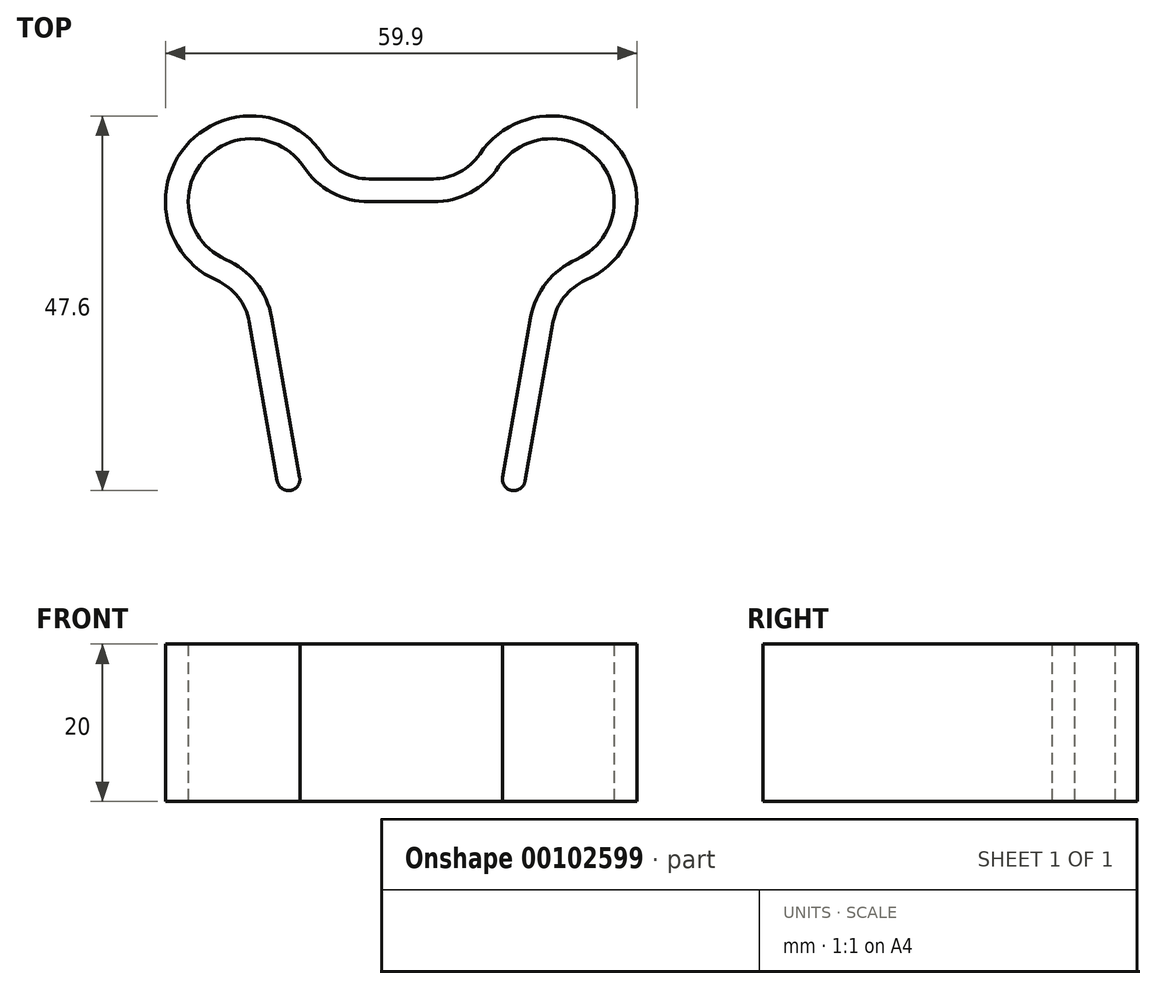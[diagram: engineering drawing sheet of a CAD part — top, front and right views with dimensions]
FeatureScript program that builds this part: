
annotation { "Feature Type Name" : "Feature", "Feature Type Description" : "" }
export const myFeature = defineFeature(function(context is Context, id is Id, definition is map)
    precondition{}
    {
        {
            var Q0;
            Q0=qCreatedBy(makeId("Top.planeOp"),FACE);
            var sketch = newSketch(context, id + "F0", { "sketchPlane" : qUnion([Q0])});
            skLineSegment(sketch, "E0.bottom", {"start": v(-19.05, 18.35) * mm, "end": v(19.05, 18.35) * mm, "construction": true});
            skLineSegment(sketch, "E0.top", {"start": v(-19.05, -18.35) * mm, "end": v(19.05, -18.35) * mm, "construction": true});
            skLineSegment(sketch, "E0.left", {"start": v(-19.05, 18.35) * mm, "end": v(-19.05, -18.35) * mm, "construction": true});
            skLineSegment(sketch, "E0.right", {"start": v(19.05, 18.35) * mm, "end": v(19.05, -18.35) * mm, "construction": true});
            skPoint(sketch, "E0.middle", {"position": v(0, 0) * mm});
            skLineSegment(sketch, "E1", {"start": v(0, 0) * mm, "end": v(0, 18.35) * mm, "construction": true});
            skLineSegment(sketch, "E2", {"start": v(0, 18.35) * mm, "end": v(-4.08, 18.35) * mm});
            skArc(sketch, "E3", {"start": v(-12.4, 22.8) * mm, "mid": v(-25.18, 23.5) * mm, "end": v(-22.27, 11.03) * mm});
            skLineSegment(sketch, "E4", {"start": v(-16.45, 3.61) * mm, "end": v(-12.88, -16.65) * mm});
            skArc(sketch, "E5", {"start": v(-15.73, -17.15) * mm, "mid": v(-14.05, -18.33) * mm, "end": v(-12.88, -16.65) * mm});
            skPoint(sketch, "E6.visualSharp", {"position": v(-19.56, 20.86) * mm});
            skPoint(sketch, "E7.visualSharp", {"position": v(-17.66, 10.47) * mm});
            skArc(sketch, "E7.filletArc", {"start": v(-16.45, 3.61) * mm, "mid": v(-18.43, 8.05) * mm, "end": v(-22.27, 11.03) * mm});
            skPoint(sketch, "E8.visualSharp", {"position": v(-11.05, 18.35) * mm});
            skArc(sketch, "E8.filletArc", {"start": v(-12.4, 22.8) * mm, "mid": v(-8.8, 19.53) * mm, "end": v(-4.08, 18.35) * mm});
            skPoint(sketch, "E9.visualSharp", {"position": v(-9, 35.61) * mm});
            skLineSegment(sketch, "E10", {"start": v(-19.05, 18.35) * mm, "end": v(-12.88, -16.65) * mm, "construction": true});
            skLineSegment(sketch, "E11", {"start": v(-15.73, -17.15) * mm, "end": v(-12.88, -16.65) * mm, "construction": true});
            skLineSegment(sketch, "E12.0", {"start": v(-19.3, 3.1) * mm, "end": v(-15.73, -17.15) * mm});
            skLineSegment(sketch, "E12.1", {"start": v(0, 21.25) * mm, "end": v(-4.08, 21.25) * mm});
            skArc(sketch, "E12.2", {"start": v(-9.99, 24.4) * mm, "mid": v(-7.43, 22.09) * mm, "end": v(-4.08, 21.25) * mm});
            skArc(sketch, "E12.3", {"start": v(-9.99, 24.4) * mm, "mid": v(-27.4, 25.36) * mm, "end": v(-23.44, 8.37) * mm});
            skArc(sketch, "E12.4", {"start": v(-19.3, 3.1) * mm, "mid": v(-20.71, 6.26) * mm, "end": v(-23.44, 8.37) * mm});
            skLineSegment(sketch, "E13.MirrorCS", {"start": v(15.73, -17.15) * mm, "end": v(12.88, -16.65) * mm, "construction": true});
            skArc(sketch, "E14.MirrorCS", {"start": v(9.99, 24.4) * mm, "mid": v(27.4, 25.36) * mm, "end": v(23.44, 8.37) * mm});
            skArc(sketch, "E15.MirrorCS", {"start": v(9.99, 24.4) * mm, "mid": v(7.43, 22.09) * mm, "end": v(4.08, 21.25) * mm});
            skLineSegment(sketch, "E16.MirrorCS", {"start": v(0, 21.25) * mm, "end": v(4.08, 21.25) * mm});
            skPoint(sketch, "E17.MirrorP", {"position": v(19.56, 20.86) * mm});
            skArc(sketch, "E18.MirrorCS", {"start": v(19.3, 3.1) * mm, "mid": v(20.71, 6.26) * mm, "end": v(23.44, 8.37) * mm});
            skPoint(sketch, "E19.MirrorP", {"position": v(17.66, 10.47) * mm});
            skLineSegment(sketch, "E20.MirrorCS", {"start": v(19.3, 3.1) * mm, "end": v(15.73, -17.15) * mm});
            skPoint(sketch, "E21.MirrorP", {"position": v(11.05, 18.35) * mm});
            skLineSegment(sketch, "E22.MirrorCS", {"start": v(0, 18.35) * mm, "end": v(4.08, 18.35) * mm});
            skArc(sketch, "E23.MirrorCS", {"start": v(12.4, 22.8) * mm, "mid": v(25.18, 23.5) * mm, "end": v(22.27, 11.03) * mm});
            skArc(sketch, "E24.MirrorCS", {"start": v(12.4, 22.8) * mm, "mid": v(8.8, 19.53) * mm, "end": v(4.08, 18.35) * mm});
            skPoint(sketch, "E25.MirrorP", {"position": v(9, 35.61) * mm});
            skLineSegment(sketch, "E26.MirrorCS", {"start": v(16.45, 3.61) * mm, "end": v(12.88, -16.65) * mm});
            skArc(sketch, "E27.MirrorCS", {"start": v(15.73, -17.15) * mm, "mid": v(14.05, -18.33) * mm, "end": v(12.88, -16.65) * mm});
            skArc(sketch, "E28.MirrorCS", {"start": v(16.45, 3.61) * mm, "mid": v(18.43, 8.05) * mm, "end": v(22.27, 11.03) * mm});
            skSolve(sketch);
        }
        {
            var Q0;
            Q0 = qSketchRegion(id + "F0", true);
            extrude(context, id + "F1", {"entities" : qUnion([Q0]), "depth" : 20 * mm});
        }
    });
